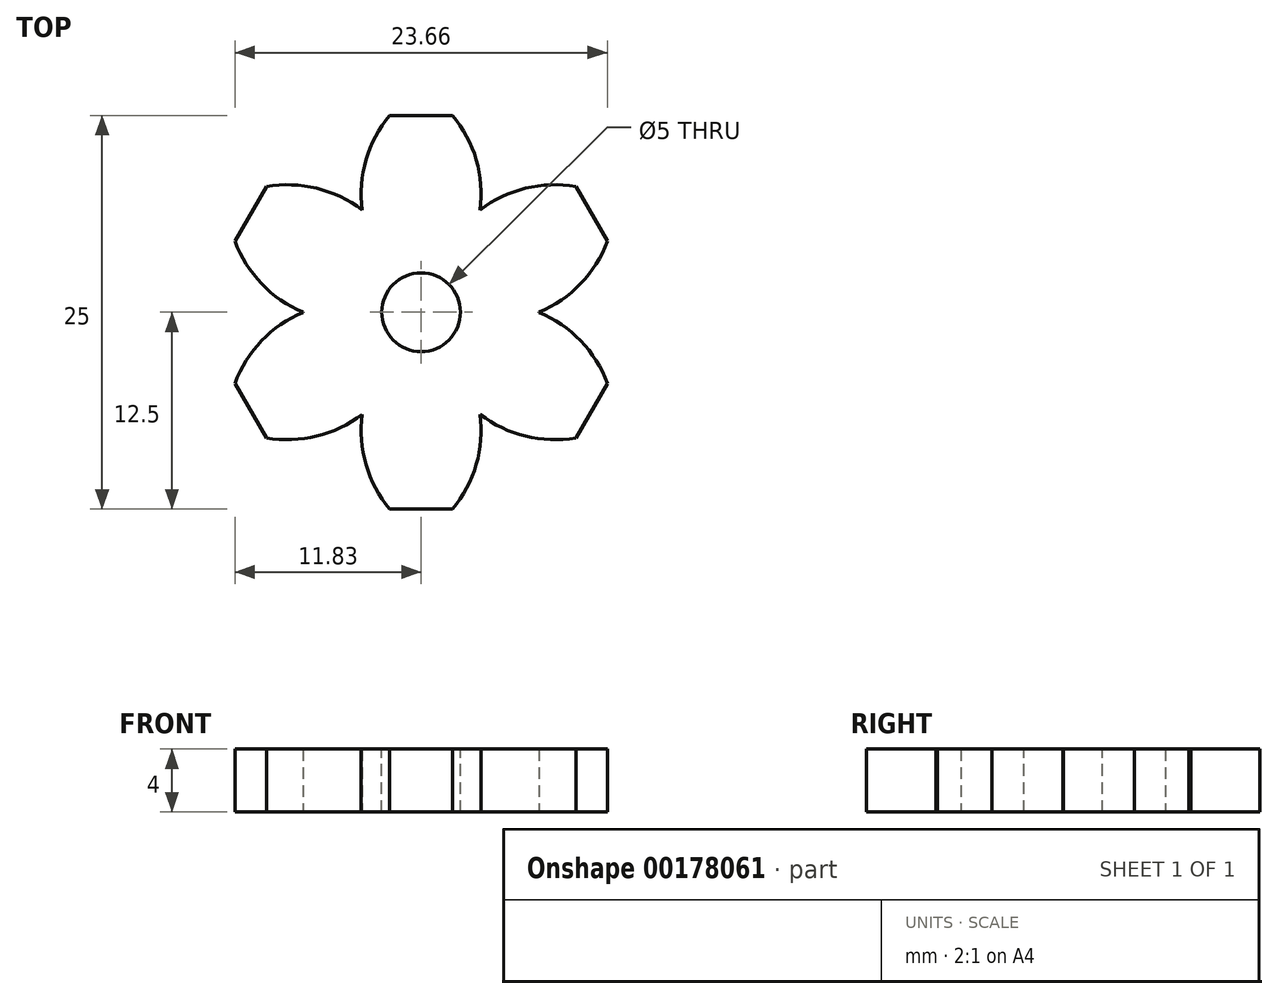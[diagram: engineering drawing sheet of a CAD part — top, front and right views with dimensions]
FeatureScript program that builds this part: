
annotation { "Feature Type Name" : "Feature", "Feature Type Description" : "" }
export const myFeature = defineFeature(function(context is Context, id is Id, definition is map)
    precondition{}
    {
        {
            var Q0;
            Q0=qCreatedBy(makeId("Top.planeOp"),FACE);
            var sketch = newSketch(context, id + "F0", { "sketchPlane" : qUnion([Q0])});
            skCircle(sketch, "E0", {"center": v(0, 0) * mm, "radius": 7.5 * mm});
            skLineSegment(sketch, "E1", {"start": v(0, 0) * mm, "end": v(0, 7.5) * mm, "construction": true});
            skLineSegment(sketch, "E2", {"start": v(0, 12.5) * mm, "end": v(-2, 12.5) * mm});
            skArc(sketch, "E3", {"start": v(-2, 12.5) * mm, "mid": v(-3.5, 9.68) * mm, "end": v(-3.75, 6.5) * mm});
            skLineSegment(sketch, "E4.MirrorCS", {"start": v(0, 12.5) * mm, "end": v(2, 12.5) * mm});
            skArc(sketch, "E5.MirrorCS", {"start": v(2, 12.5) * mm, "mid": v(3.5, 9.68) * mm, "end": v(3.75, 6.5) * mm});
            skArc(sketch, "E6.1.0", {"start": v(-11.83, 4.52) * mm, "mid": v(-10.13, 1.8) * mm, "end": v(-7.5, 0) * mm});
            skLineSegment(sketch, "E6.1.1", {"start": v(-10.83, 6.25) * mm, "end": v(-11.83, 4.52) * mm});
            skLineSegment(sketch, "E6.1.2", {"start": v(-10.83, 6.25) * mm, "end": v(-9.83, 7.98) * mm});
            skArc(sketch, "E6.1.3", {"start": v(-9.83, 7.98) * mm, "mid": v(-6.63, 7.87) * mm, "end": v(-3.75, 6.5) * mm});
            skArc(sketch, "E6.2.0", {"start": v(-9.83, -7.98) * mm, "mid": v(-6.63, -7.87) * mm, "end": v(-3.75, -6.5) * mm});
            skLineSegment(sketch, "E6.2.1", {"start": v(-10.83, -6.25) * mm, "end": v(-9.83, -7.98) * mm});
            skLineSegment(sketch, "E6.2.2", {"start": v(-10.83, -6.25) * mm, "end": v(-11.83, -4.52) * mm});
            skArc(sketch, "E6.2.3", {"start": v(-11.83, -4.52) * mm, "mid": v(-10.13, -1.8) * mm, "end": v(-7.5, 0) * mm});
            skArc(sketch, "E6.3.0", {"start": v(2, -12.5) * mm, "mid": v(3.5, -9.68) * mm, "end": v(3.75, -6.5) * mm});
            skLineSegment(sketch, "E6.3.1", {"start": v(0, -12.5) * mm, "end": v(2, -12.5) * mm});
            skLineSegment(sketch, "E6.3.2", {"start": v(0, -12.5) * mm, "end": v(-2, -12.5) * mm});
            skArc(sketch, "E6.3.3", {"start": v(-2, -12.5) * mm, "mid": v(-3.5, -9.68) * mm, "end": v(-3.75, -6.5) * mm});
            skArc(sketch, "E6.4.0", {"start": v(11.83, -4.52) * mm, "mid": v(10.13, -1.8) * mm, "end": v(7.5, 0) * mm});
            skLineSegment(sketch, "E6.4.1", {"start": v(10.83, -6.25) * mm, "end": v(11.83, -4.52) * mm});
            skLineSegment(sketch, "E6.4.2", {"start": v(10.83, -6.25) * mm, "end": v(9.83, -7.98) * mm});
            skArc(sketch, "E6.4.3", {"start": v(9.83, -7.98) * mm, "mid": v(6.63, -7.87) * mm, "end": v(3.75, -6.5) * mm});
            skArc(sketch, "E6.5.0", {"start": v(9.83, 7.98) * mm, "mid": v(6.63, 7.87) * mm, "end": v(3.75, 6.5) * mm});
            skLineSegment(sketch, "E6.5.1", {"start": v(10.83, 6.25) * mm, "end": v(9.83, 7.98) * mm});
            skLineSegment(sketch, "E6.5.2", {"start": v(10.83, 6.25) * mm, "end": v(11.83, 4.52) * mm});
            skArc(sketch, "E6.5.3", {"start": v(11.83, 4.52) * mm, "mid": v(10.13, 1.8) * mm, "end": v(7.5, 0) * mm});
            skSolve(sketch);
        }
        {
            var Q0;
            Q0 = qSketchRegion(id + "F0", true);
            extrude(context, id + "F1", {"entities" : qUnion([Q0]), "depth" : 4 * mm});
        }
        {
            var Q0;
            Q0=makeQuery(id+"F1.opExtrude","CAP_FACE",FACE,{"disambiguationData":[OSD([sQuery(id+"F0.wireOp",EDGE,"E0"),sQuery(id+"F0.wireOp",EDGE,"E2"),sQuery(id+"F0.wireOp",EDGE,"E3"),sQuery(id+"F0.wireOp",EDGE,"E4.MirrorCS"),sQuery(id+"F0.wireOp",EDGE,"E5.MirrorCS"),sQuery(id+"F0.wireOp",EDGE,"E6.1.0"),sQuery(id+"F0.wireOp",EDGE,"E6.1.1"),sQuery(id+"F0.wireOp",EDGE,"E6.1.2"),sQuery(id+"F0.wireOp",EDGE,"E6.1.3"),sQuery(id+"F0.wireOp",EDGE,"E6.2.0"),sQuery(id+"F0.wireOp",EDGE,"E6.2.1"),sQuery(id+"F0.wireOp",EDGE,"E6.2.2"),sQuery(id+"F0.wireOp",EDGE,"E6.2.3"),sQuery(id+"F0.wireOp",EDGE,"E6.3.0"),sQuery(id+"F0.wireOp",EDGE,"E6.3.1"),sQuery(id+"F0.wireOp",EDGE,"E6.3.2"),sQuery(id+"F0.wireOp",EDGE,"E6.3.3"),sQuery(id+"F0.wireOp",EDGE,"E6.4.0"),sQuery(id+"F0.wireOp",EDGE,"E6.4.1"),sQuery(id+"F0.wireOp",EDGE,"E6.4.2"),sQuery(id+"F0.wireOp",EDGE,"E6.4.3"),sQuery(id+"F0.wireOp",EDGE,"E6.5.0"),sQuery(id+"F0.wireOp",EDGE,"E6.5.1"),sQuery(id+"F0.wireOp",EDGE,"E6.5.2"),sQuery(id+"F0.wireOp",EDGE,"E6.5.3"),sQuery(id+"F0.wireOp",EDGE,"E6.6.0"),sQuery(id+"F0.wireOp",EDGE,"E6.6.1"),sQuery(id+"F0.wireOp",EDGE,"E6.6.2"),sQuery(id+"F0.wireOp",EDGE,"E6.6.3")])],"isStart":false});
            var sketch = newSketch(context, id + "F2", { "sketchPlane" : qUnion([Q0])});
            skCircle(sketch, "E7", {"center": v(0, 0) * mm, "radius": 2.5 * mm});
            skSolve(sketch);
        }
        {
            var Q0;
            Q0 = qSketchRegion(id + "F2", true);
            extrude(context, id + "F3", {"entities" : qUnion([Q0]), "operationType" : NewBodyOperationType.REMOVE, "endBound" : BoundingType.THROUGH_ALL, "oppositeDirection" : true, "depth" : 25 * mm});
        }
    });
